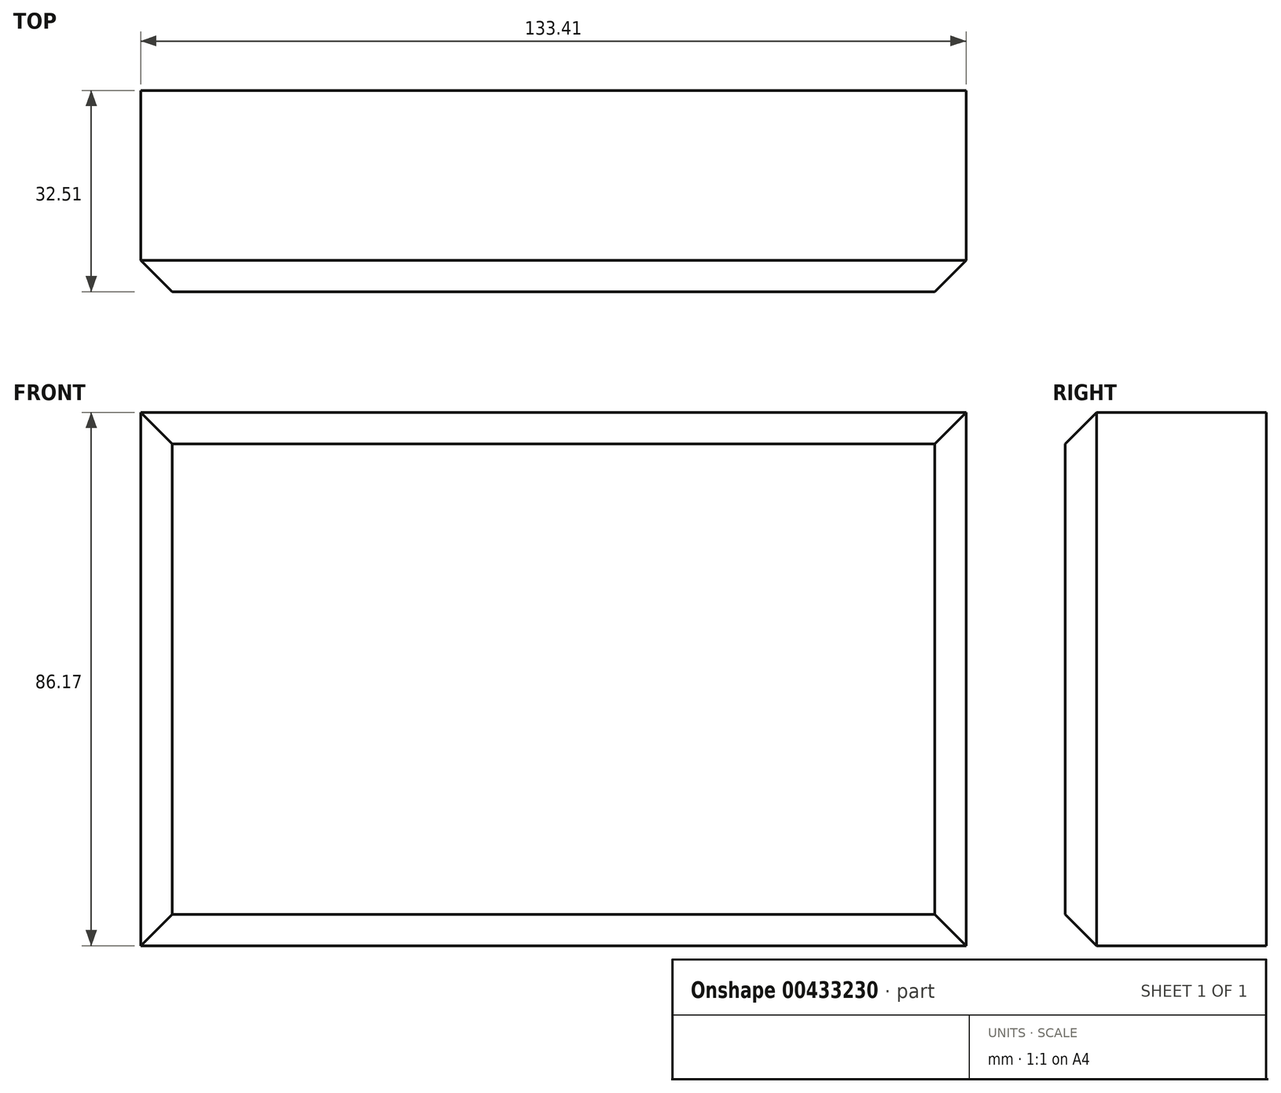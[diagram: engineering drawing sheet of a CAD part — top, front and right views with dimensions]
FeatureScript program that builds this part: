
annotation { "Feature Type Name" : "Feature", "Feature Type Description" : "" }
export const myFeature = defineFeature(function(context is Context, id is Id, definition is map)
    precondition{}
    {
        {
            var Q0;
            Q0=qCreatedBy(makeId("Front.planeOp"),FACE);
            var sketch = newSketch(context, id + "F0", { "sketchPlane" : qUnion([Q0])});
            skLineSegment(sketch, "E0.bottom", {"start": v(-64.72, 37.13) * mm, "end": v(68.7, 37.13) * mm});
            skLineSegment(sketch, "E0.top", {"start": v(-64.72, -49.04) * mm, "end": v(68.7, -49.04) * mm});
            skLineSegment(sketch, "E0.left", {"start": v(-64.72, 37.13) * mm, "end": v(-64.72, -49.04) * mm});
            skLineSegment(sketch, "E0.right", {"start": v(68.7, 37.13) * mm, "end": v(68.7, -49.04) * mm});
            skSolve(sketch);
        }
        {
            var Q0;
            Q0 = qSketchRegion(id + "F0", true);
            extrude(context, id + "F1", {"entities" : qUnion([Q0]), "depth" : 32.5 * mm});
        }
        {
            var Q0;
            Q0=makeQuery(id+"F1.opExtrude","CAP_EDGE",EDGE,{"disambiguationData":[OSD([sQuery(id+"F0.wireOp",EDGE,"E0.top")])],"isStart":false});
            var Q1;
            Q1=makeQuery(id+"F1.opExtrude","CAP_EDGE",EDGE,{"disambiguationData":[OSD([sQuery(id+"F0.wireOp",EDGE,"E0.left")])],"isStart":false});
            var Q2;
            Q2=makeQuery(id+"F1.opExtrude","CAP_EDGE",EDGE,{"disambiguationData":[OSD([sQuery(id+"F0.wireOp",EDGE,"E0.right")])],"isStart":false});
            var Q3;
            Q3=makeQuery(id+"F1.opExtrude","CAP_EDGE",EDGE,{"disambiguationData":[OSD([sQuery(id+"F0.wireOp",EDGE,"E0.bottom")])],"isStart":false});
            var Q4;
            Q4=makeQuery(id+"F1.opExtrude","CAP_FACE",FACE,{"disambiguationData":[OSD([sQuery(id+"F0.wireOp",EDGE,"E0.bottom"),sQuery(id+"F0.wireOp",EDGE,"E0.top"),sQuery(id+"F0.wireOp",EDGE,"E0.left"),sQuery(id+"F0.wireOp",EDGE,"E0.right")])],"isStart":false});
            chamfer(context, id + "F2", {"entities" : qUnion([Q0, Q1, Q2, Q3, Q4]), "width" : 5.08 * mm, "tangentPropagation" : true});
        }
    });
